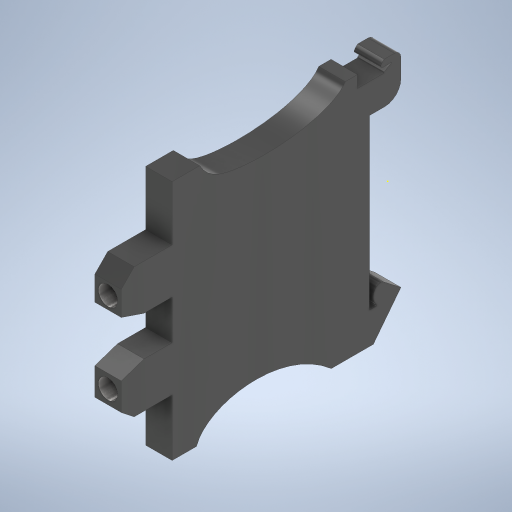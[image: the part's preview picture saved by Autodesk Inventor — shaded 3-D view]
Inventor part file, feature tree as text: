
AUTODESK INVENTOR PART (.ipt)
format: ipt  version: 2023 (Build 270158000, 158)  size: 368,128 bytes
history: native  units: in
note: dims shown in document units (in); Inventor stores cm internally (conversion verified against a paired STEP export)
features: sketch x10, other x5, extrude x4, fillet x2
ambient origin geometry x8: Origin, YZ Plane, XZ Plane, XY Plane, X Axis, Y Axis, Z Axis, Center Point
bodies: Solid1 (feature_tree)
feature tree (21):
  sketch  "Sketch1"  dims[d0=0.2047in d1=1.8701in]
  extrude  "Extrusion1"  Depth=1.8701in
  extrude  "Extrusion2"  Depth=0.3937in
  fillet  "Fillet1"  Radius=0.35in
  fillet  "Fillet2"  Radius=0.3937in
  extrude  "Extrusion3"  Depth=1.9685in TaperAngle=0.0deg
  extrude  "Extrusion4"  Depth=1.9685in TaperAngle=0.0deg
  sketch  "Sketch2"  dims[d2=1.7717in d3=0.0in d4=0.35in d5=0.35in d6=0.3937in d7=0.0in]
  sketch  "Sketch3"  dims[d8=0.12in d9=1.9685in d10=0.0in]
  sketch  "Sketch4"  dims[d11=1.9685in d12=0.0in d13=1.9685in d14=0.0in]
  sketch  "Sketch5"  dims[d15=1.9685in d16=0.0in]
  sketch  "Sketch6"  dims[d17=0.125in]
  sketch  "Sketch7"  dims[d18=0.05in]
  sketch  "Sketch8"  dims[d19=1.9685in d20=0.0in]
  sketch  "Sketch9"  dims[d21=0.15in]
  sketch  "Sketch10"  dims[d22=0.2756in d23=0.0in d24=0.15in d25=0.2756in d26=0.0in]
  other  "Cut1"
  other  "Cut2"
  other  "Cut3"
  other  "Cut4"
  other  "Cut5"
